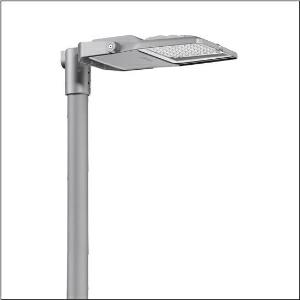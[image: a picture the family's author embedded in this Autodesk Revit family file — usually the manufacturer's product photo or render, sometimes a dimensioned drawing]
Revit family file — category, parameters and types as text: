
# Revit family: floodlight_fl_21_iq_mini___pl52_5xa7772c2d3a_4b1a
name_source: partatom
category: Lighting Fixtures
units: mm (PartAtom-declared; Revit-internal decimal feet)

## family parameters
Cut with Voids When Loaded = No
Host = Face
Light Source = No
Part Type = Normal
Room Calculation Point = No
Round Connector Dimension = Use Diameter
Shared = No

## types (1)
- --- (1 x LED, 12210 lm, 87.2 W, 3000K)
    Apparent Load = 87 VA
    CIE Flux Codes = 26 60 98 100 100
    Color Rendering = 70
    Color Temperature = 3000K
    Default Elevation = 1800 mm
    Description = Floodlight FL 21 iQ mini, floodlight, primary light control with lens, of PMMA, primary optical cover: protective disc, of toughened safety glass, transparent, light distribution: PL52, light emission: direct distribution, installation type: surface-mounted, LED, High Power LED, rated luminous flux: 12.210lm, luminous efficacy: 140lm/W, light colour: 730, colour temperature: 3000K, control: Auto-Match, Temp-Guard, Night-Set, Smart-Wire, Desk-Remote (wireless, voltage-free reading and setting of iQ features in the workshop via application-optimized NFC function/RFID function), optimised constant luminous flux control (CLO 2.0), Light-Fading, Lumen-Switch, with terminal, 6-pole, mains connection: 220..240V, AC, 50/60Hz, start of lifetime: 87W, end of service life: 92W, reduction: 40W, luminaire housing, of diecast aluminium, powder-coated, Siteco® metallic grey (DB 702S), corrosivity category C5 mid according to DIN EN ISO 12944, sealing non-destructively replaceable, please order mast flange separately, mast bracket, of steel, galvanised, powder-coated, protection rating (complete): IP66, insulation class (complete): insulation class II (safety insulation), certification: CE, ENEC, VDE, protection symbol: D, impact resistance: IK08, permissible operating ambient temperature: -40..+40°C, permissible operating ambient temperature for outdoor applications: -40..+50°C, standard: DIN EN 12944, LABS conformity tested according to VDMA 24364:2018-05, packaging unit: 1 piece

Light Distribution: PL52
    Height = 70 mm
    Lamp = 1 x LED
    Lamp Light Flux = 12210 lm
    Lamp Power = 87.2 W
    Lamp count = 1
    Length = 485 mm
    Luminous efficacy = 140 lm/W
    Manufacturer = Siteco
    ModVariant = No
    Model = 5XA7772C2D3A
    Number of Poles = 1
    OnlyDefault = Yes
    Power Factor = 1
    Product Name = Floodlight FL 21 iQ mini | PL52
    Product group = floodlight | pylon annexe
    ProductGroupID = 6200
    Protection Class = Protection class II
    Protection Degree = IP 66
    RLX_Detail_Level = 1
    RLX_Emergency_Light_Flux = 0 lm
    RLX_Emergency_Type = 0
    RLX_Emergency_Type_DB = No
    RlxData = <blob elided: 101549 chars, md5=a0670d7f>
    Socket = socket
    Standby Power = 0 W
    System Light Flux = 12210 lm
    System Power = 87 W
    Type Comments = factory setting: luminous flux: 100 % | dim-lin: 254 | 456 mA
    Type Image = l_1007125.jpg
    URL = http://relux.com
    VarID = @adj_096603
    Voltage = 0 V
    Weight = 0.00 kg
    Width = 337 mm

## geometry (parser evidence)
native form markers: Blend x4, Sweep x12
no freeform markers — native parametric forms only
